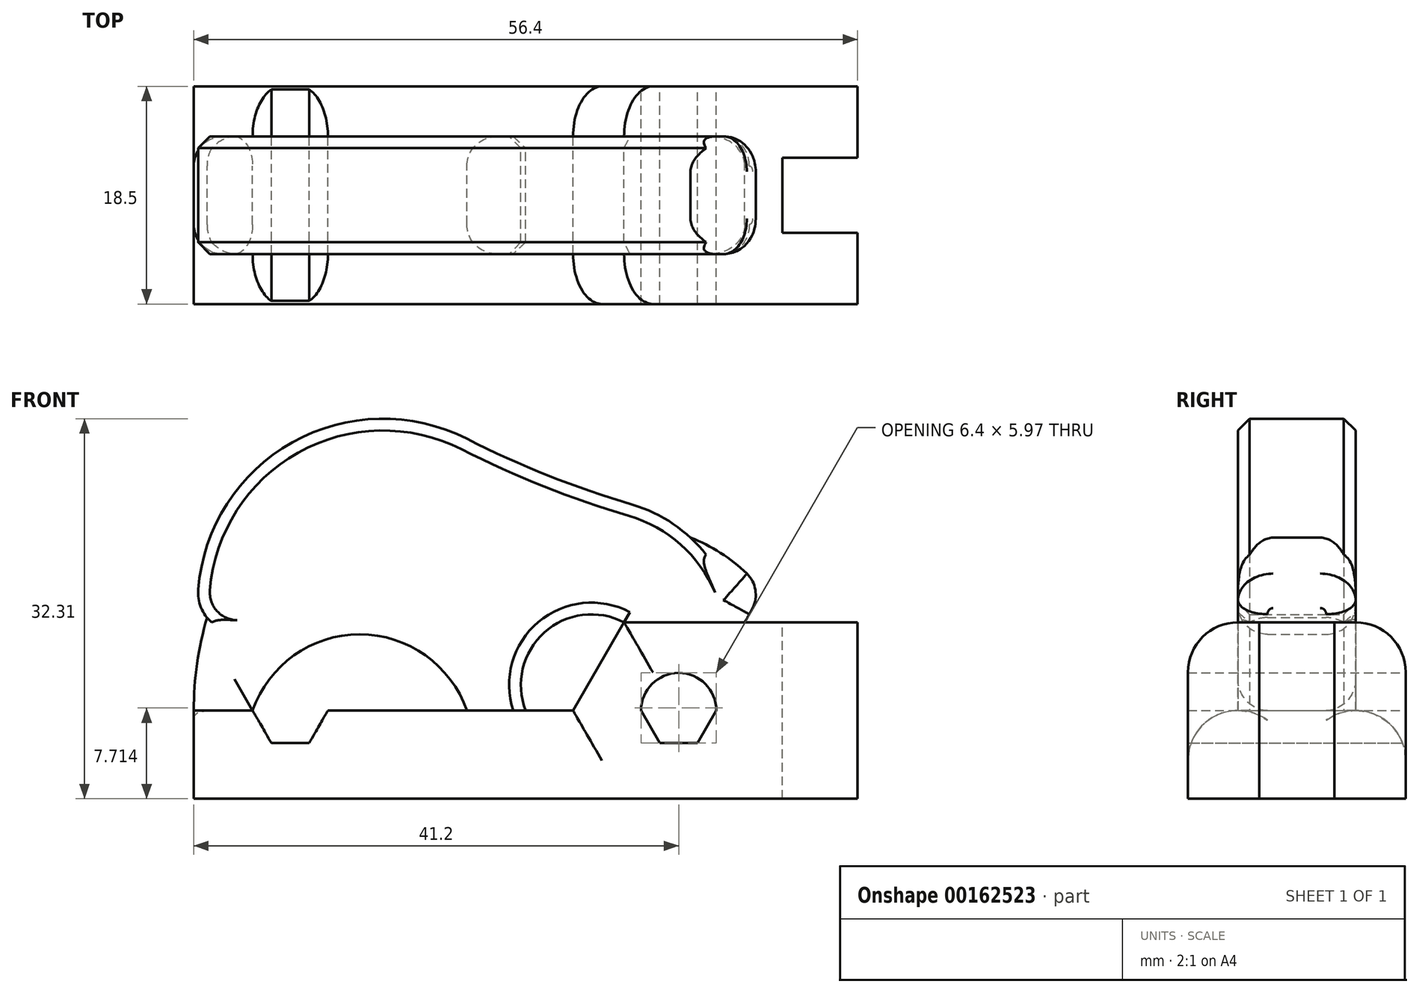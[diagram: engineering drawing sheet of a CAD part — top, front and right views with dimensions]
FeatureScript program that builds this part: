
annotation { "Feature Type Name" : "Feature", "Feature Type Description" : "" }
export const myFeature = defineFeature(function(context is Context, id is Id, definition is map)
    precondition{}
    {
        {
            var Q0;
            Q0=qCreatedBy(makeId("Front.planeOp"),FACE);
            var sketch = newSketch(context, id + "F0", { "sketchPlane" : qUnion([Q0])});
            skLineSegment(sketch, "E0", {"start": v(28.2, 0) * mm, "end": v(28.2, -7.5) * mm});
            skLineSegment(sketch, "E1", {"start": v(28.2, -7.5) * mm, "end": v(0, -7.5) * mm});
            skLineSegment(sketch, "E2.MirrorCS", {"start": v(-28.2, -7.5) * mm, "end": v(0, -7.5) * mm});
            skLineSegment(sketch, "E3.MirrorCS", {"start": v(-28.2, 0) * mm, "end": v(-28.2, -7.5) * mm});
            skLineSegment(sketch, "E4", {"start": v(28.2, 0) * mm, "end": v(28.2, 7.5) * mm});
            skLineSegment(sketch, "E5", {"start": v(28.2, 7.5) * mm, "end": v(13.2, 7.5) * mm});
            skArc(sketch, "E6", {"start": v(13.2, 7.5) * mm, "mid": v(-3.88, 14.68) * mm, "end": v(-15.18, 0) * mm, "construction": true});
            skLineSegment(sketch, "E7", {"start": v(-28.2, 0) * mm, "end": v(-23.2, 0) * mm});
            skLineSegment(sketch, "E8.trimOffspring", {"start": v(-16.8, 0) * mm, "end": v(-15.18, 0) * mm});
            skCircle(sketch, "E9", {"center": v(13, 0) * mm, "radius": 2.5 * mm, "construction": true});
            skPoint(sketch, "E9.centerSnap0", {"position": v(14.1, -7.5) * mm});
            skCircle(sketch, "E10.cCircle", {"center": v(-20, 0) * mm, "radius": 2.77 * mm, "construction": true});
            skLineSegment(sketch, "E10.0", {"start": v(-18.4, -2.77) * mm, "end": v(-21.6, -2.77) * mm});
            skLineSegment(sketch, "E10.1", {"start": v(-21.6, -2.77) * mm, "end": v(-23.2, 0) * mm});
            skLineSegment(sketch, "E10.2", {"start": v(-23.2, 0) * mm, "end": v(-21.6, 2.77) * mm, "construction": true});
            skLineSegment(sketch, "E10.3", {"start": v(-21.6, 2.77) * mm, "end": v(-18.4, 2.77) * mm, "construction": true});
            skLineSegment(sketch, "E10.4", {"start": v(-18.4, 2.77) * mm, "end": v(-16.8, 0) * mm, "construction": true});
            skLineSegment(sketch, "E10.5", {"start": v(-16.8, 0) * mm, "end": v(-18.4, -2.77) * mm});
            skPoint(sketch, "E10.0.midPoint", {"position": v(-20, -2.77) * mm});
            skCircle(sketch, "E11.cCircle", {"center": v(13, 0) * mm, "radius": 2.77 * mm, "construction": true});
            skLineSegment(sketch, "E11.0", {"start": v(11.4, 2.77) * mm, "end": v(14.6, 2.77) * mm, "construction": true});
            skLineSegment(sketch, "E11.1", {"start": v(14.6, 2.77) * mm, "end": v(16.2, 0) * mm, "construction": true});
            skLineSegment(sketch, "E11.2", {"start": v(16.2, 0) * mm, "end": v(14.6, -2.77) * mm});
            skLineSegment(sketch, "E11.3", {"start": v(14.6, -2.77) * mm, "end": v(11.4, -2.77) * mm});
            skLineSegment(sketch, "E11.4", {"start": v(11.4, -2.77) * mm, "end": v(9.8, 0) * mm});
            skLineSegment(sketch, "E11.5", {"start": v(9.8, 0) * mm, "end": v(11.4, 2.77) * mm, "construction": true});
            skPoint(sketch, "E11.0.midPoint", {"position": v(13, 2.77) * mm});
            skArc(sketch, "E12", {"start": v(9.8, 0) * mm, "mid": v(13, 3.2) * mm, "end": v(16.2, 0) * mm});
            skLineSegment(sketch, "E13", {"start": v(-15.18, 0) * mm, "end": v(4.03, 0) * mm});
            skLineSegment(sketch, "E14", {"start": v(4.03, 0) * mm, "end": v(8.36, 7.5) * mm});
            skLineSegment(sketch, "E15", {"start": v(8.36, 7.5) * mm, "end": v(13.2, 7.5) * mm});
            skSolve(sketch);
        }
        {
            var Q0;
            Q0 = qSketchRegion(id + "F0", true);
            extrude(context, id + "F1", {"entities" : qUnion([Q0]), "endBound" : BoundingType.SYMMETRIC, "depth" : 18.5 * mm, "offsetDistance" : 25 * mm});
        }
        {
            var Q0;
            Q0=makeQuery(id+"F1.opExtrude","SWEPT_FACE",FACE,{"disambiguationData":[OSD([sQuery(id+"F0.wireOp",EDGE,"E5")])]});
            var sketch = newSketch(context, id + "F2", { "sketchPlane" : qUnion([Q0])});
            skLineSegment(sketch, "E16.bottom", {"start": v(28.2, -3.2) * mm, "end": v(21.8, -3.2) * mm});
            skLineSegment(sketch, "E16.top", {"start": v(28.2, 3.2) * mm, "end": v(21.8, 3.2) * mm});
            skLineSegment(sketch, "E16.left", {"start": v(28.2, -3.2) * mm, "end": v(28.2, 3.2) * mm});
            skLineSegment(sketch, "E16.right", {"start": v(21.8, -3.2) * mm, "end": v(21.8, 3.2) * mm});
            skPoint(sketch, "E16.middle", {"position": v(25, 0) * mm});
            skSolve(sketch);
        }
        {
            var Q0;
            Q0 = qSketchRegion(id + "F2", true);
            extrude(context, id + "F3", {"entities" : qUnion([Q0]), "operationType" : NewBodyOperationType.REMOVE, "oppositeDirection" : true, "depth" : 25 * mm});
        }
        {
            var Q0;
            Q0=qCreatedBy(makeId("Front.planeOp"),FACE);
            var sketch = newSketch(context, id + "F4", { "sketchPlane" : qUnion([Q0])});
            skArc(sketch, "E17", {"start": v(-28.2, 0) * mm, "mid": v(-27.92, 4) * mm, "end": v(-27.07, 7.9) * mm});
            skLineSegment(sketch, "E18", {"start": v(18.6, 7.5) * mm, "end": v(8.36, 7.5) * mm});
            skLineSegment(sketch, "E19", {"start": v(0, 0) * mm, "end": v(-5, 0) * mm});
            skArc(sketch, "E20", {"start": v(-16.8, 0) * mm, "mid": v(-20, 3.2) * mm, "end": v(-23.2, 0) * mm, "construction": true});
            skLineSegment(sketch, "E21", {"start": v(-28.2, 0) * mm, "end": v(-23.2, 0) * mm});
            skLineSegment(sketch, "E22", {"start": v(-27.07, 7.9) * mm, "end": v(-27.07, 7.9) * mm});
            skArc(sketch, "E23", {"start": v(-27.82, 10.3) * mm, "mid": v(-27.68, 9.03) * mm, "end": v(-27.07, 7.9) * mm});
            skArc(sketch, "E24", {"start": v(-5, 23.1) * mm, "mid": v(-19.83, 22.8) * mm, "end": v(-27.82, 10.3) * mm});
            skArc(sketch, "E25", {"start": v(-5, 23.1) * mm, "mid": v(1.91, 19.99) * mm, "end": v(9.08, 17.5) * mm});
            skArc(sketch, "E26", {"start": v(14, 14.7) * mm, "mid": v(11.7, 16.38) * mm, "end": v(9.08, 17.5) * mm});
            skArc(sketch, "E27", {"start": v(20, 10.3) * mm, "mid": v(17.3, 12.9) * mm, "end": v(14, 14.7) * mm});
            skArc(sketch, "E28", {"start": v(18.6, 7.5) * mm, "mid": v(19.35, 8.88) * mm, "end": v(20, 10.3) * mm});
            skPoint(sketch, "E29.start.orphan", {"position": v(21.8, 7.5) * mm});
            skArc(sketch, "E30", {"start": v(8.36, 7.5) * mm, "mid": v(1.58, 6.64) * mm, "end": v(0, 0) * mm});
            skArc(sketch, "E31", {"start": v(-5, 0) * mm, "mid": v(-10, 5) * mm, "end": v(-15, 0) * mm, "construction": true});
            skLineSegment(sketch, "E32.trimOffspring", {"start": v(-15, 0) * mm, "end": v(-16.8, 0) * mm, "construction": true});
            skArc(sketch, "E33", {"start": v(-5, 0) * mm, "mid": v(-14.1, 6.48) * mm, "end": v(-23.2, 0) * mm});
            skSolve(sketch);
        }
        {
            var Q0;
            Q0 = qSketchRegion(id + "F4", true);
            extrude(context, id + "F5", {"entities" : qUnion([Q0]), "operationType" : NewBodyOperationType.ADD, "endBound" : BoundingType.SYMMETRIC, "depth" : 10 * mm, "offsetDistance" : 25 * mm});
        }
        {
            var Q0;
            Q0=makeQuery(id+"F1.opExtrude","CAP_EDGE",EDGE,{"disambiguationData":[OSD([sQuery(id+"F0.wireOp",EDGE,"E8.trimOffspring"),sQuery(id+"F0.wireOp",EDGE,"E13")])],"isStart":false});
            var Q1;
            Q1=makeQuery(id+"F1.opExtrude","CAP_EDGE",EDGE,{"disambiguationData":[OSD([sQuery(id+"F0.wireOp",EDGE,"E8.trimOffspring"),sQuery(id+"F0.wireOp",EDGE,"E13")])],"isStart":true});
            var Q2;
            Q2=makeQuery(id+"F1.opExtrude","CAP_EDGE",EDGE,{"disambiguationData":[OSD([sQuery(id+"F0.wireOp",EDGE,"E14")])],"isStart":false});
            var Q3;
            Q3=makeQuery(id+"F1.opExtrude","CAP_EDGE",EDGE,{"disambiguationData":[OSD([sQuery(id+"F0.wireOp",EDGE,"E14")])],"isStart":true});
            var Q4;
            Q4=makeQuery(id+"F1.opExtrude","CAP_EDGE",EDGE,{"disambiguationData":[OSD([sQuery(id+"F0.wireOp",EDGE,"E5"),sQuery(id+"F0.wireOp",EDGE,"E15")])],"isStart":false});
            var Q5;
            Q5=makeQuery(id+"F1.opExtrude","CAP_EDGE",EDGE,{"disambiguationData":[OSD([sQuery(id+"F0.wireOp",EDGE,"E5"),sQuery(id+"F0.wireOp",EDGE,"E15")])],"isStart":true});
            fillet(context, id + "F6", {"entities" : qUnion([Q0, Q1, Q2, Q3, Q4, Q5]), "radius" : 4.25 * mm, "tangentPropagation" : true, "allowEdgeOverflow" : false});
        }
        {
            var Q0;
            Q0=makeQuery(id+"F5.opExtrude","CAP_EDGE",EDGE,{"disambiguationData":[OSD([sQuery(id+"F4.wireOp",EDGE,"E27")])],"isStart":false});
            var Q1;
            Q1=makeQuery(id+"F5.opExtrude","CAP_EDGE",EDGE,{"disambiguationData":[OSD([sQuery(id+"F4.wireOp",EDGE,"E27")])],"isStart":true});
            fillet(context, id + "F7", {"entities" : qUnion([Q0, Q1]), "radius" : 3 * mm, "tangentPropagation" : true, "allowEdgeOverflow" : false});
        }
        {
            var Q0;
            Q0=makeQuery(id+"F5.opExtrude","CAP_EDGE",EDGE,{"disambiguationData":[OSD([sQuery(id+"F4.wireOp",EDGE,"E33")])],"isStart":false});
            var Q1;
            Q1=makeQuery(id+"F5.opExtrude","CAP_EDGE",EDGE,{"disambiguationData":[OSD([sQuery(id+"F4.wireOp",EDGE,"E33")])],"isStart":true});
            fillet(context, id + "F8", {"entities" : qUnion([Q0, Q1]), "radius" : 2.5 * mm, "tangentPropagation" : true, "allowEdgeOverflow" : false});
        }
        {
            var Q0;
            Q0=makeQuery(id+"F5.opExtrude","CAP_EDGE",EDGE,{"disambiguationData":[OSD([sQuery(id+"F4.wireOp",EDGE,"E25")])],"isStart":false});
            var Q1;
            Q1=makeQuery(id+"F5.opExtrude","CAP_EDGE",EDGE,{"disambiguationData":[OSD([sQuery(id+"F4.wireOp",EDGE,"E24")])],"isStart":false});
            var Q2;
            Q2=makeQuery(id+"F5.opExtrude","CAP_EDGE",EDGE,{"disambiguationData":[OSD([sQuery(id+"F4.wireOp",EDGE,"E23")])],"isStart":false});
            var Q3;
            Q3=makeQuery(id+"F5.opExtrude","CAP_EDGE",EDGE,{"disambiguationData":[OSD([sQuery(id+"F4.wireOp",EDGE,"E25")])],"isStart":true});
            var Q4;
            Q4=makeQuery(id+"F5.opExtrude","CAP_EDGE",EDGE,{"disambiguationData":[OSD([sQuery(id+"F4.wireOp",EDGE,"E30")])],"isStart":false});
            var Q5;
            Q5=makeQuery(id+"F5.opExtrude","CAP_EDGE",EDGE,{"disambiguationData":[OSD([sQuery(id+"F4.wireOp",EDGE,"E30")])],"isStart":true});
            chamfer(context, id + "F9", {"entities" : qUnion([Q0, Q1, Q2, Q3, Q4, Q5]), "width" : 1 * mm, "tangentPropagation" : true});
        }
        {
            var Q0;
            Q0=makeQuery(id+"F5.opExtrude","CAP_EDGE",EDGE,{"disambiguationData":[OSD([sQuery(id+"F4.wireOp",EDGE,"E17")])],"isStart":false});
            var Q1;
            Q1=makeQuery(id+"F5.opExtrude","CAP_EDGE",EDGE,{"disambiguationData":[OSD([sQuery(id+"F4.wireOp",EDGE,"E17")])],"isStart":true});
            fillet(context, id + "F10", {"entities" : qUnion([Q0, Q1]), "radius" : 2.5 * mm, "tangentPropagation" : true, "allowEdgeOverflow" : false});
        }
        {
            var Q0;
            Q0=makeQuery(id+"F5.opExtrude","SWEPT_EDGE",EDGE,{"disambiguationData":[OSD([sQuery(id+"F4.wireOp",EDGE,"E27"),sQuery(id+"F4.wireOp",EDGE,"E28")])]});
            fillet(context, id + "F11", {"entities" : qUnion([Q0]), "radius" : 2.5 * mm, "tangentPropagation" : true, "allowEdgeOverflow" : false});
        }
    });
